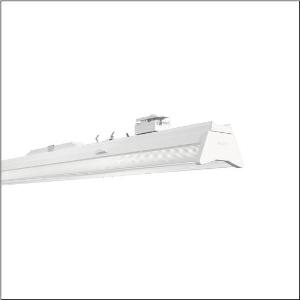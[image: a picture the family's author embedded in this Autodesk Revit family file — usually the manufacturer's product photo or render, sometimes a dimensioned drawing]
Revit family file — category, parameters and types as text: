
# Revit family: licross_r__21_performance_mo_52td16cn49xg_b518
name_source: partatom
category: Lighting Fixtures
units: mm (PartAtom-declared; Revit-internal decimal feet)

## family parameters
Cut with Voids When Loaded = No
Host = Face
Light Source = No
Part Type = Normal
Room Calculation Point = No
Round Connector Dimension = Use Diameter
Shared = No

## types (1)
- --- (1 x LED, 9240 lm, 50.4 W, 4000K)
    Apparent Load = 50 VA
    CIE Flux Codes = 66 88 96 79 100
    Color Rendering = 80
    Color Temperature = 4000K
    Default Elevation = 1800 mm
    Description = Licross® 21 Performance MO, luminaire insert, of sheet steel, galvanised, coil coated, white, length: 1.500mm, width: 120mm, height: 123mm, LED rated luminous flux: 9.240lm, light colour: 840, control gear: ON/OFF Multilumen, CLOi, control gear: ECG Multilumen, with plug, 3-pole, with phase selection, mains connection: 220..240V, AC, 50/60Hz, start of lifetime: 50W, end of service life: 61W, halogen-free wiring, primary light control with lens, of plastic, primary optical cover: cover, of PMMA, light emission: direct/indirect distribution, primary light characteristic: symmetric, protection rating (complete): IP54, insulation class (complete): insulation class I (protective earthing), certification: CE, ENEC, UKCA, protection symbol: D if used in an environment with non-conductive dust loads with corresponding accessories, impact resistance: IK06, permissible ambient temperature for indoor applications: -35..+45°C, corresponds to IFS (International Featured Standards) requirements for safety and quality in the food industry, reducing of maximum allowable ambient temperature of 5°C with ceiling mounting, LABS conformity tested according to VDMA 24364:2018-05, packaging unit: 1 piece
    Height = 114 mm
    Lamp = 1 x LED
    Lamp Light Flux = 9240 lm
    Lamp Power = 50.4 W
    Lamp count = 1
    Length = 1500 mm
    Luminous efficacy = 183 lm/W
    Manufacturer = Siteco
    ModVariant = No
    Model = 52TD16CN49XG
    Mounting Place = Ceiling
    Mounting Type = Pendant
    Number of Poles = 1
    OnlyDefault = Yes
    Power Factor = 1
    Product Name = Licross® 21 Performance MO
    Product group = luminaire insert
    ProductGroupID = 901
    Protection Class = Protection class I
    Protection Degree = IP 54
    RLX_Detail_Level = 1
    RLX_Emergency_Light_Flux = 0 lm
    RLX_Emergency_Type = 0
    RLX_Emergency_Type_DB = No
    RlxData = <blob elided: 31917 chars, md5=8e368981>
    Socket = socket
    Standby Power = 0 W
    System Light Flux = 9240 lm
    System Power = 50 W
    Type Comments = factory setting: luminous flux: 100 % | (A | C | E) | 117 mA
    Type Image = l_1256138.jpg
    URL = http://relux.com
    VarID = @adj_041649
    Voltage = 0 V
    Weight = 0.00 kg
    Width = 120 mm

## geometry (parser evidence)
native form markers: Blend x4, Sweep x12
no freeform markers — native parametric forms only
